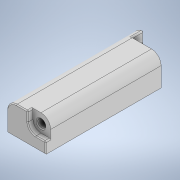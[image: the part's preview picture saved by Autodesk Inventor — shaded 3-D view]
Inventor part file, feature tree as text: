
AUTODESK INVENTOR PART (.ipt)
format: ipt  version: 2022 (Build 260153000, 153)  size: 196,096 bytes
history: native  units: mm
features: fillet x5, sketch x5, extrude x4, chamfer x2, hole x1
ambient origin geometry x8: Origin, YZ Plane, XZ Plane, XY Plane, X Axis, Y Axis, Z Axis, Center Point
bodies: Solid1 (feature_tree)
feature tree (17):
  extrude  "Extrusion1"  Depth=25.4mm
  extrude  "Extrusion2"  Depth=11.621mm
  extrude  "Extrusion3"  Depth=3.429mm TaperAngle=0.0deg
  hole  "Hole1"  [1 undecoded]
  fillet  "Fillet1"  Radius=7.938mm
  fillet  "Fillet2"  Radius=6.35mm
  fillet  "Fillet3"  Radius=6.35mm
  fillet  "Fillet4"  Radius=6.35mm
  chamfer  "Chamfer1"  Distance=0.794mm
  extrude  "Extrusion4"  Depth=5.271mm
  fillet  "Fillet5"  Radius=13.208mm
  chamfer  "Chamfer2"  Distance=0.6mm Angle=45.0deg
  sketch  "Sketch1"  dims[d0=25.4mm d1=25.4mm]
  sketch  "Sketch2"  dims[d2=84.138mm d3=0.0mm d4=11.621mm]
  sketch  "Sketch3"  dims[d5=11.621mm d6=3.429mm d7=0.0mm]
  sketch  "Sketch4"  dims[d8=19.558mm d9=19.558mm d10=7.938mm d11=0.0mm d12=6.35mm d13=6.35mm]
  sketch  "Sketch5"  dims[d14=5.334mm d15=6.0mm d16=9.779mm d17=2.0mm d18=14.3117mm d19=8.0mm d20=20.594885mm d21=6.35mm d22=0.794mm d23=5.271mm d24=13.208mm d25=0.6mm d26=2.0mm d27=45.0deg d28=6.35mm d29=25.4mm d30=84.138mm d31=0.0mm d32=0.794mm d33=0.6mm d34=2.0mm d35=45.0deg]
note: 1 required parameter value undecoded (feature->parameter linkage not recoverable at this tier; creation-order binding heuristic only, values carry confidence <= 0.55)
